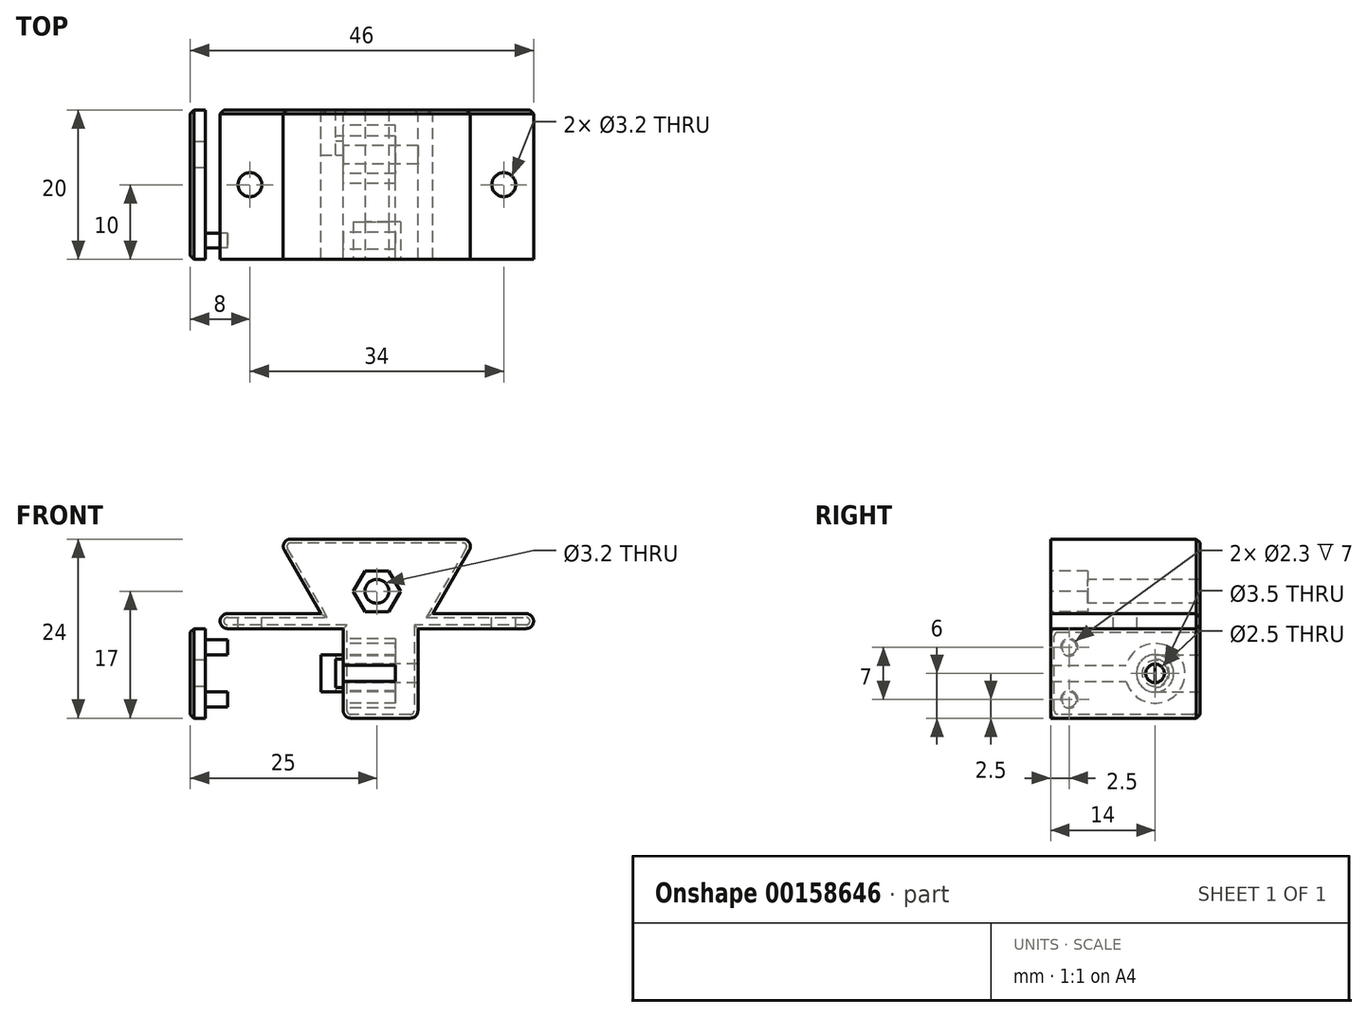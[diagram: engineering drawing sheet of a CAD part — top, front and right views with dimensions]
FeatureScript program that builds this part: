
annotation { "Feature Type Name" : "Feature", "Feature Type Description" : "" }
export const myFeature = defineFeature(function(context is Context, id is Id, definition is map)
    precondition{}
    {
        {
            var Q0;
            Q0=qCreatedBy(makeId("Front.planeOp"),FACE);
            var sketch = newSketch(context, id + "F0", { "sketchPlane" : qUnion([Q0])});
            skLineSegment(sketch, "E0", {"start": v(-7.5, 1) * mm, "end": v(-12.4, 9.5) * mm});
            skLineSegment(sketch, "E1", {"start": v(-11.54, 11) * mm, "end": v(11.54, 11) * mm});
            skLineSegment(sketch, "E2", {"start": v(12.4, 9.5) * mm, "end": v(7.5, 1) * mm});
            skPoint(sketch, "E3.visualSharp", {"position": v(-13.27, 11) * mm});
            skArc(sketch, "E3.filletArc", {"start": v(-11.54, 11) * mm, "mid": v(-12.4, 10.5) * mm, "end": v(-12.4, 9.5) * mm});
            skPoint(sketch, "E4.visualSharp", {"position": v(13.27, 11) * mm});
            skArc(sketch, "E4.filletArc", {"start": v(12.4, 9.5) * mm, "mid": v(12.4, 10.5) * mm, "end": v(11.54, 11) * mm});
            skLineSegment(sketch, "E5.bottom", {"start": v(21, -1) * mm, "end": v(-21, -1) * mm});
            skLineSegment(sketch, "E5.top", {"start": v(21, 1) * mm, "end": v(-21, 1) * mm});
            skLineSegment(sketch, "E5.left", {"start": v(21, -1) * mm, "end": v(21, 1) * mm});
            skLineSegment(sketch, "E5.right", {"start": v(-21, -1) * mm, "end": v(-21, 1) * mm});
            skPoint(sketch, "E5.middle", {"position": v(0, 0) * mm});
            skLineSegment(sketch, "E6.bottom", {"start": v(5.5, -13) * mm, "end": v(-4.5, -13) * mm});
            skLineSegment(sketch, "E6.top", {"start": v(5.5, -1) * mm, "end": v(-4.5, -1) * mm});
            skLineSegment(sketch, "E6.left", {"start": v(5.5, -13) * mm, "end": v(5.5, -1) * mm});
            skLineSegment(sketch, "E6.right", {"start": v(-4.5, -13) * mm, "end": v(-4.5, -1) * mm});
            skSolve(sketch);
        }
        {
            var Q0;
            Q0 = qSketchRegion(id + "F0", true);
            extrude(context, id + "F1", {"entities" : qUnion([Q0]), "depth" : 20 * mm});
        }
        {
            var Q0;
            Q0=makeQuery(id+"F1.opExtrude","SWEPT_FACE",FACE,{"disambiguationData":[OSD([sQuery(id+"F0.wireOp",EDGE,"E6.right")])]});
            var sketch = newSketch(context, id + "F2", { "sketchPlane" : qUnion([Q0])});
            skLineSegment(sketch, "E7", {"start": v(20, -7) * mm, "end": v(6, -7) * mm, "construction": true});
            skCircle(sketch, "E8", {"center": v(6, -7) * mm, "radius": 2.5 * mm});
            skCircle(sketch, "E9", {"center": v(6, -7) * mm, "radius": 4 * mm});
            skLineSegment(sketch, "E10.bottom", {"start": v(20, -8.1) * mm, "end": v(9.85, -8.1) * mm});
            skLineSegment(sketch, "E10.top", {"start": v(20, -5.9) * mm, "end": v(9.85, -5.9) * mm});
            skLineSegment(sketch, "E10.left", {"start": v(20, -8.1) * mm, "end": v(20, -5.9) * mm});
            skLineSegment(sketch, "E10.right", {"start": v(9.85, -8.1) * mm, "end": v(9.85, -5.9) * mm});
            skPoint(sketch, "E10.middle", {"position": v(14.92, -7) * mm});
            skCircle(sketch, "E11", {"center": v(17.5, -10.5) * mm, "radius": 1.15 * mm});
            skCircle(sketch, "E12.MirrorC", {"center": v(17.5, -3.5) * mm, "radius": 1.15 * mm});
            skSolve(sketch);
        }
        {
            var Q0;
            Q0 = qSketchRegion(id + "F2", true);
            extrude(context, id + "F3", {"entities" : qUnion([Q0]), "operationType" : NewBodyOperationType.REMOVE, "oppositeDirection" : true, "depth" : 7 * mm});
        }
        {
            var Q0;
            Q0=makeQuery(id+"F3.boolean.opBoolean","SPLIT",FACE,{"disambiguationData":[TD([makeQuery(id+"F3.opExtrude","SWEPT_FACE",FACE,{"disambiguationData":[OSD([sQuery(id+"F2.wireOp",EDGE,"E8")])]})])],"derivedFrom":makeQuery(id+"F1.opExtrude","SWEPT_FACE",FACE,{"disambiguationData":[OSD([sQuery(id+"F0.wireOp",EDGE,"E6.right")])]})});
            var sketch = newSketch(context, id + "F4", { "sketchPlane" : qUnion([Q0])});
            skCircle(sketch, "E13", {"center": v(6, -7) * mm, "radius": 1.25 * mm});
            skSolve(sketch);
        }
        {
            var Q0;
            Q0 = qSketchRegion(id + "F4", true);
            extrude(context, id + "F5", {"entities" : qUnion([Q0]), "operationType" : NewBodyOperationType.REMOVE, "endBound" : BoundingType.THROUGH_ALL, "oppositeDirection" : true, "depth" : 25 * mm});
        }
        {
            var Q0;
            Q0=makeQuery(id+"F3.boolean.opBoolean","SPLIT",FACE,{"disambiguationData":[TD([makeQuery(id+"F3.opExtrude","SWEPT_FACE",FACE,{"disambiguationData":[OSD([sQuery(id+"F2.wireOp",EDGE,"E8")])]})])],"derivedFrom":makeQuery(id+"F1.opExtrude","SWEPT_FACE",FACE,{"disambiguationData":[OSD([sQuery(id+"F0.wireOp",EDGE,"E6.right")])]})});
            var sketch = newSketch(context, id + "F6", { "sketchPlane" : qUnion([Q0])});
            skArc(sketch, "E14", {"start": v(6, -4.5) * mm, "mid": v(3.5, -7) * mm, "end": v(6, -9.5) * mm});
            skArc(sketch, "E15", {"start": v(6, -5.1) * mm, "mid": v(4.1, -7) * mm, "end": v(6, -8.9) * mm});
            skLineSegment(sketch, "E16", {"start": v(6, -8.9) * mm, "end": v(6, -9.5) * mm});
            skLineSegment(sketch, "E17", {"start": v(6, -4.5) * mm, "end": v(6, -5.1) * mm});
            skSolve(sketch);
        }
        {
            var Q0;
            Q0 = qSketchRegion(id + "F6", true);
            extrude(context, id + "F7", {"entities" : qUnion([Q0]), "operationType" : NewBodyOperationType.ADD, "depth" : 1 * mm});
        }
        {
            var Q0;
            Q0=makeQuery(id+"F7.opExtrude","CAP_FACE",FACE,{"disambiguationData":[OSD([sQuery(id+"F6.wireOp",EDGE,"E14"),sQuery(id+"F6.wireOp",EDGE,"E15"),sQuery(id+"F6.wireOp",EDGE,"E16"),sQuery(id+"F6.wireOp",EDGE,"E17")])],"isStart":false});
            var sketch = newSketch(context, id + "F8", { "sketchPlane" : qUnion([Q0])});
            skLineSegment(sketch, "E18.bottom", {"start": v(6, -4.5) * mm, "end": v(0, -4.5) * mm});
            skLineSegment(sketch, "E18.top", {"start": v(6, -9.5) * mm, "end": v(0, -9.5) * mm});
            skLineSegment(sketch, "E18.left", {"start": v(6, -4.5) * mm, "end": v(6, -9.5) * mm});
            skLineSegment(sketch, "E18.right", {"start": v(0, -4.5) * mm, "end": v(0, -9.5) * mm});
            skSolve(sketch);
        }
        {
            var Q0;
            Q0 = qSketchRegion(id + "F8", true);
            extrude(context, id + "F9", {"entities" : qUnion([Q0]), "operationType" : NewBodyOperationType.ADD, "depth" : 2 * mm});
        }
        {
            var Q0;
            Q0=qCreatedBy(makeId("Right.planeOp"),FACE);
            cPlane(context, id + "F10", {"entities" : qUnion([Q0]), "cplaneType" : CPlaneType.OFFSET, "offset" : 25 * mm, "oppositeDirection" : true, "width" : 150 * mm, "height" : 150 * mm});
        }
        {
            var Q0;
            Q0=qCreatedBy(id+"F10.planeOp",FACE);
            var sketch = newSketch(context, id + "F11", { "sketchPlane" : qUnion([Q0])});
            skLineSegment(sketch, "E19.bottom", {"start": v(-20, -1) * mm, "end": v(0, -1) * mm});
            skLineSegment(sketch, "E19.top", {"start": v(-20, -13) * mm, "end": v(0, -13) * mm});
            skLineSegment(sketch, "E19.left", {"start": v(-20, -1) * mm, "end": v(-20, -13) * mm});
            skLineSegment(sketch, "E19.right", {"start": v(0, -1) * mm, "end": v(0, -13) * mm});
            skCircle(sketch, "E20", {"center": v(-6, -7) * mm, "radius": 1.75 * mm});
            skSolve(sketch);
        }
        {
            var Q0;
            Q0 = qSketchRegion(id + "F11", true);
            extrude(context, id + "F12", {"entities" : qUnion([Q0]), "depth" : 2 * mm});
        }
        {
            var Q0;
            Q0=makeQuery(id+"F12.opExtrude","CAP_FACE",FACE,{"disambiguationData":[OSD([sQuery(id+"F11.wireOp",EDGE,"E19.bottom"),sQuery(id+"F11.wireOp",EDGE,"E19.top"),sQuery(id+"F11.wireOp",EDGE,"E19.left"),sQuery(id+"F11.wireOp",EDGE,"E19.right"),sQuery(id+"F11.wireOp",EDGE,"E20")])],"isStart":false});
            var sketch = newSketch(context, id + "F13", { "sketchPlane" : qUnion([Q0])});
            skCircle(sketch, "E21", {"center": v(-17.5, -10.5) * mm, "radius": 1 * mm});
            skCircle(sketch, "E22", {"center": v(-17.5, -3.5) * mm, "radius": 1 * mm});
            skSolve(sketch);
        }
        {
            var Q0;
            Q0 = qSketchRegion(id + "F13", true);
            extrude(context, id + "F14", {"entities" : qUnion([Q0]), "operationType" : NewBodyOperationType.ADD, "depth" : 3 * mm});
        }
        {
            var Q0;
            {var subQ0=sQuery(id+"F0.wireOp",EDGE,"E5.top");Q0=makeQuery(id+"F1.opExtrude","SWEPT_FACE",FACE,{"disambiguationData":[OSD([subQ0]),TDD([makeQuery(id+"F0.imprint","IMPRINT",EDGE,{"disambiguationData":[TD([[makeQuery(id+"F0.imprint","INTERSECT",VERTEX,{"derivedFrom":[sQuery(id+"F0.wireOp",EDGE,"E0"),subQ0]}),-1.0]])],"derivedFrom":subQ0})])]});}
            var sketch = newSketch(context, id + "F15", { "sketchPlane" : qUnion([Q0])});
            skCircle(sketch, "E23", {"center": v(17, -10) * mm, "radius": 1.6 * mm});
            skCircle(sketch, "E24", {"center": v(-17, -10) * mm, "radius": 1.6 * mm});
            skLineSegment(sketch, "E25", {"start": v(-21, -10) * mm, "end": v(31.4, -10) * mm, "construction": true});
            skSolve(sketch);
        }
        {
            var Q0;
            Q0 = qSketchRegion(id + "F15", true);
            extrude(context, id + "F16", {"entities" : qUnion([Q0]), "operationType" : NewBodyOperationType.REMOVE, "endBound" : BoundingType.THROUGH_ALL, "oppositeDirection" : true, "depth" : 25 * mm});
        }
        {
            var Q0;
            Q0=makeQuery(id+"F1.opExtrude","CAP_FACE",FACE,{"disambiguationData":[OSD([sQuery(id+"F0.wireOp",EDGE,"E0"),sQuery(id+"F0.wireOp",EDGE,"E1"),sQuery(id+"F0.wireOp",EDGE,"E2"),sQuery(id+"F0.wireOp",EDGE,"E3.filletArc"),sQuery(id+"F0.wireOp",EDGE,"E4.filletArc"),sQuery(id+"F0.wireOp",EDGE,"E5.bottom"),sQuery(id+"F0.wireOp",EDGE,"E5.top"),sQuery(id+"F0.wireOp",EDGE,"E5.left"),sQuery(id+"F0.wireOp",EDGE,"E5.right"),sQuery(id+"F0.wireOp",EDGE,"E6.bottom"),sQuery(id+"F0.wireOp",EDGE,"E6.left"),sQuery(id+"F0.wireOp",EDGE,"E6.right")])],"isStart":false});
            var sketch = newSketch(context, id + "F17", { "sketchPlane" : qUnion([Q0])});
            skCircle(sketch, "E26.cCircle", {"center": v(0, 4) * mm, "radius": 2.75 * mm, "construction": true});
            skLineSegment(sketch, "E26.0", {"start": v(1.59, 1.25) * mm, "end": v(-1.59, 1.25) * mm});
            skLineSegment(sketch, "E26.1", {"start": v(-1.59, 1.25) * mm, "end": v(-3.18, 4) * mm});
            skLineSegment(sketch, "E26.2", {"start": v(-3.18, 4) * mm, "end": v(-1.59, 6.75) * mm});
            skLineSegment(sketch, "E26.3", {"start": v(-1.59, 6.75) * mm, "end": v(1.59, 6.75) * mm});
            skLineSegment(sketch, "E26.4", {"start": v(1.59, 6.75) * mm, "end": v(3.18, 4) * mm});
            skLineSegment(sketch, "E26.5", {"start": v(3.18, 4) * mm, "end": v(1.59, 1.25) * mm});
            skPoint(sketch, "E26.0.midPoint", {"position": v(0, 1.25) * mm});
            skSolve(sketch);
        }
        {
            var Q0;
            Q0 = qSketchRegion(id + "F17", true);
            extrude(context, id + "F18", {"entities" : qUnion([Q0]), "operationType" : NewBodyOperationType.REMOVE, "oppositeDirection" : true, "depth" : 5 * mm});
        }
        {
            var Q0;
            Q0=makeQuery(id+"F18.boolean.opBoolean","COPY",FACE,{"derivedFrom":makeQuery(id+"F18.opExtrude","CAP_FACE",FACE,{"disambiguationData":[OSD([sQuery(id+"F17.wireOp",EDGE,"E26.0"),sQuery(id+"F17.wireOp",EDGE,"E26.1"),sQuery(id+"F17.wireOp",EDGE,"E26.2"),sQuery(id+"F17.wireOp",EDGE,"E26.3"),sQuery(id+"F17.wireOp",EDGE,"E26.4"),sQuery(id+"F17.wireOp",EDGE,"E26.5")])],"isStart":false})});
            var sketch = newSketch(context, id + "F19", { "sketchPlane" : qUnion([Q0])});
            skCircle(sketch, "E27", {"center": v(0, 4) * mm, "radius": 1.6 * mm});
            skSolve(sketch);
        }
        {
            var Q0;
            Q0 = qSketchRegion(id + "F19", true);
            extrude(context, id + "F20", {"entities" : qUnion([Q0]), "operationType" : NewBodyOperationType.REMOVE, "endBound" : BoundingType.THROUGH_ALL, "oppositeDirection" : true, "depth" : 25 * mm});
        }
        {
            var Q0;
            Q0=makeQuery(id+"F1.opExtrude","SWEPT_EDGE",EDGE,{"disambiguationData":[OSD([sQuery(id+"F0.wireOp",EDGE,"E6.bottom"),sQuery(id+"F0.wireOp",EDGE,"E6.left")])]});
            var Q1;
            Q1=makeQuery(id+"F1.opExtrude","SWEPT_EDGE",EDGE,{"disambiguationData":[OSD([sQuery(id+"F0.wireOp",EDGE,"E5.bottom"),sQuery(id+"F0.wireOp",EDGE,"E5.left")])]});
            var Q2;
            Q2=makeQuery(id+"F1.opExtrude","SWEPT_EDGE",EDGE,{"disambiguationData":[OSD([sQuery(id+"F0.wireOp",EDGE,"E5.top"),sQuery(id+"F0.wireOp",EDGE,"E5.left")])]});
            var Q3;
            Q3=makeQuery(id+"F1.opExtrude","SWEPT_EDGE",EDGE,{"disambiguationData":[OSD([sQuery(id+"F0.wireOp",EDGE,"E5.bottom"),sQuery(id+"F0.wireOp",EDGE,"E5.right")])]});
            var Q4;
            Q4=makeQuery(id+"F1.opExtrude","SWEPT_EDGE",EDGE,{"disambiguationData":[OSD([sQuery(id+"F0.wireOp",EDGE,"E5.top"),sQuery(id+"F0.wireOp",EDGE,"E5.right")])]});
            var Q5;
            Q5=makeQuery(id+"F1.opExtrude","SWEPT_EDGE",EDGE,{"disambiguationData":[OSD([sQuery(id+"F0.wireOp",EDGE,"E6.bottom"),sQuery(id+"F0.wireOp",EDGE,"E6.right")])]});
            var Q6;
            Q6=makeQuery(id+"F12.opExtrude","SWEPT_EDGE",EDGE,{"disambiguationData":[OSD([sQuery(id+"F11.wireOp",EDGE,"E19.bottom"),sQuery(id+"F11.wireOp",EDGE,"E19.left")])]});
            var Q7;
            Q7=makeQuery(id+"F12.opExtrude","SWEPT_EDGE",EDGE,{"disambiguationData":[OSD([sQuery(id+"F11.wireOp",EDGE,"E19.bottom"),sQuery(id+"F11.wireOp",EDGE,"E19.right")])]});
            var Q8;
            Q8=makeQuery(id+"F12.opExtrude","SWEPT_EDGE",EDGE,{"disambiguationData":[OSD([sQuery(id+"F11.wireOp",EDGE,"E19.top"),sQuery(id+"F11.wireOp",EDGE,"E19.left")])]});
            var Q9;
            Q9=makeQuery(id+"F12.opExtrude","SWEPT_EDGE",EDGE,{"disambiguationData":[OSD([sQuery(id+"F11.wireOp",EDGE,"E19.top"),sQuery(id+"F11.wireOp",EDGE,"E19.right")])]});
            fillet(context, id + "F21", {"entities" : qUnion([Q0, Q1, Q2, Q3, Q4, Q5, Q6, Q7, Q8, Q9]), "radius" : 1 * mm, "tangentPropagation" : true, "allowEdgeOverflow" : false});
        }
        {
            var Q0;
            Q0=makeQuery(id+"F1.opExtrude","CAP_EDGE",EDGE,{"disambiguationData":[OSD([sQuery(id+"F0.wireOp",EDGE,"E6.right")])],"isStart":true});
            var Q1;
            {var subQ0=sQuery(id+"F0.wireOp",EDGE,"E5.bottom");Q1=makeQuery(id+"F1.opExtrude","CAP_EDGE",EDGE,{"disambiguationData":[OSD([subQ0]),TDD([makeQuery(id+"F0.imprint","IMPRINT",EDGE,{"disambiguationData":[TD([[makeQuery(id+"F0.imprint","INTERSECT",VERTEX,{"derivedFrom":[subQ0,sQuery(id+"F0.wireOp",EDGE,"E5.right")]}),1.0]])],"derivedFrom":subQ0})])],"isStart":true});}
            var Q2;
            Q2=makeQuery(id+"F1.opExtrude","CAP_EDGE",EDGE,{"disambiguationData":[OSD([sQuery(id+"F0.wireOp",EDGE,"E0")])],"isStart":true});
            var Q3;
            {var subQ0=sQuery(id+"F0.wireOp",EDGE,"E5.bottom");Q3=makeQuery(id+"F1.opExtrude","CAP_EDGE",EDGE,{"disambiguationData":[OSD([subQ0]),TDD([makeQuery(id+"F0.imprint","IMPRINT",EDGE,{"disambiguationData":[TD([[makeQuery(id+"F0.imprint","INTERSECT",VERTEX,{"derivedFrom":[subQ0,sQuery(id+"F0.wireOp",EDGE,"E5.left")]}),-1.0]])],"derivedFrom":subQ0})])],"isStart":true});}
            var Q4;
            Q4=makeQuery(id+"F12.opExtrude","CAP_EDGE",EDGE,{"disambiguationData":[OSD([sQuery(id+"F11.wireOp",EDGE,"E19.bottom")])],"isStart":true});
            chamfer(context, id + "F22", {"entities" : qUnion([Q0, Q1, Q2, Q3, Q4]), "width" : .5 * mm, "tangentPropagation" : true});
        }
    });
